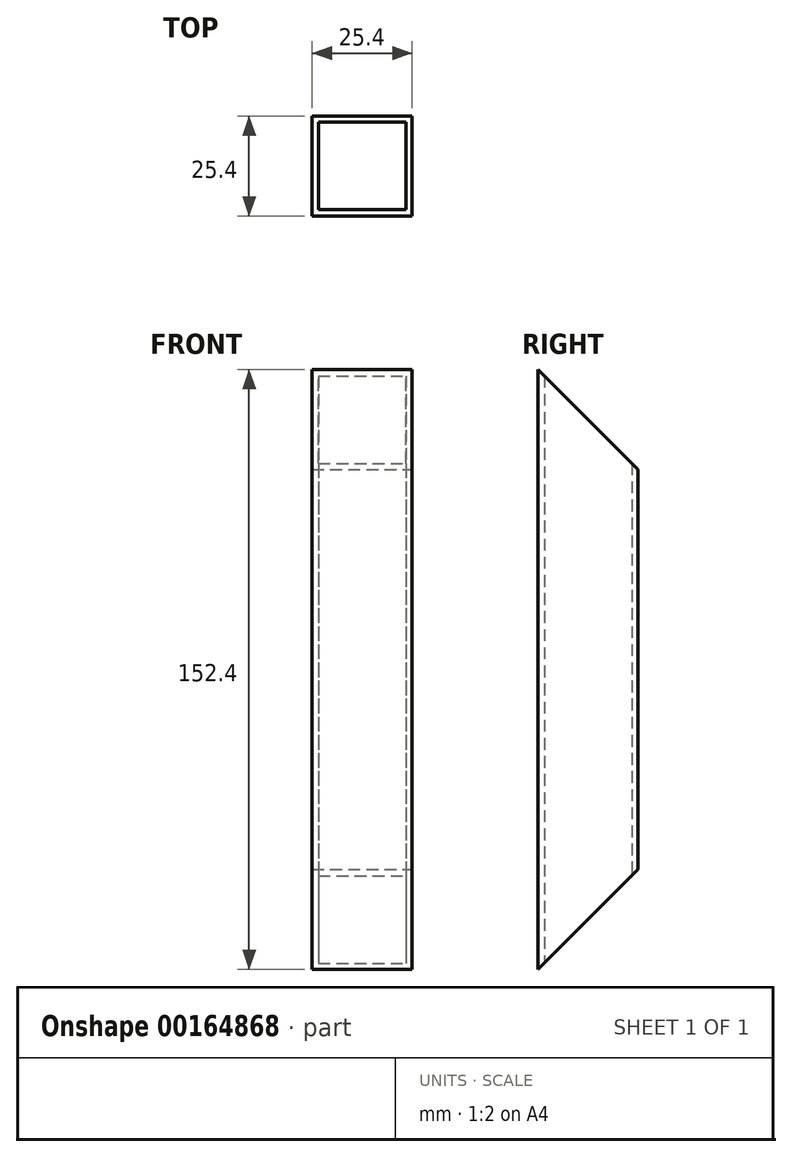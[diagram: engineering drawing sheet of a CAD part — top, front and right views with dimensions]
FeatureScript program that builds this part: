
annotation { "Feature Type Name" : "Feature", "Feature Type Description" : "" }
export const myFeature = defineFeature(function(context is Context, id is Id, definition is map)
    precondition{}
    {
        {
            var Q0;
            Q0=qCreatedBy(makeId("Top.planeOp"),FACE);
            var sketch = newSketch(context, id + "F0", { "sketchPlane" : qUnion([Q0])});
            skLineSegment(sketch, "E0.bottom", {"start": v(11.11, -11.11) * mm, "end": v(-11.11, -11.11) * mm});
            skLineSegment(sketch, "E0.top", {"start": v(11.11, 11.11) * mm, "end": v(-11.11, 11.11) * mm});
            skLineSegment(sketch, "E0.left", {"start": v(11.11, -11.11) * mm, "end": v(11.11, 11.11) * mm});
            skLineSegment(sketch, "E0.right", {"start": v(-11.11, -11.11) * mm, "end": v(-11.11, 11.11) * mm});
            skPoint(sketch, "E0.middle", {"position": v(0, 0) * mm});
            skLineSegment(sketch, "E1.bottom", {"start": v(12.7, -12.7) * mm, "end": v(-12.7, -12.7) * mm});
            skLineSegment(sketch, "E1.top", {"start": v(12.7, 12.7) * mm, "end": v(-12.7, 12.7) * mm});
            skLineSegment(sketch, "E1.left", {"start": v(12.7, -12.7) * mm, "end": v(12.7, 12.7) * mm});
            skLineSegment(sketch, "E1.right", {"start": v(-12.7, -12.7) * mm, "end": v(-12.7, 12.7) * mm});
            skSolve(sketch);
        }
        {
            var Q0;
            Q0=qSketchRegion(id+"F0",true);
            extrude(context, id + "F1", {"entities" : qUnion([Q0]), "depth" : 152.4 * mm});
        }
        {
            var Q0;
            Q0=makeQuery(id+"F1.opExtrude","SWEPT_FACE",FACE,{"disambiguationData":[OSD([sQuery(id+"F0.wireOp",EDGE,"E1.left")])]});
            var sketch = newSketch(context, id + "F2", { "sketchPlane" : qUnion([Q0])});
            skLineSegment(sketch, "E2.bottom", {"start": v(-12.7, 152.4) * mm, "end": v(12.7, 152.4) * mm});
            skLineSegment(sketch, "E2.top", {"start": v(-12.7, 127) * mm, "end": v(12.7, 127) * mm, "construction": true});
            skLineSegment(sketch, "E2.left", {"start": v(-12.7, 152.4) * mm, "end": v(-12.7, 127) * mm, "construction": true});
            skLineSegment(sketch, "E2.right", {"start": v(12.7, 152.4) * mm, "end": v(12.7, 127) * mm});
            skLineSegment(sketch, "E3", {"start": v(-12.7, 152.4) * mm, "end": v(12.7, 127) * mm});
            skLineSegment(sketch, "E4.bottom", {"start": v(-12.7, 0) * mm, "end": v(12.7, 0) * mm});
            skLineSegment(sketch, "E4.top", {"start": v(-12.7, 25.4) * mm, "end": v(12.7, 25.4) * mm, "construction": true});
            skLineSegment(sketch, "E4.left", {"start": v(-12.7, 0) * mm, "end": v(-12.7, 25.4) * mm, "construction": true});
            skLineSegment(sketch, "E4.right", {"start": v(12.7, 0) * mm, "end": v(12.7, 25.4) * mm});
            skLineSegment(sketch, "E5", {"start": v(-12.7, 0) * mm, "end": v(12.7, 25.4) * mm});
            skSolve(sketch);
        }
        {
            var Q0;
            Q0 = qSketchRegion(id + "F2", true);
            var Q1;
            Q1=makeQuery(id+"F1.opExtrude","SWEPT_FACE",FACE,{"disambiguationData":[OSD([sQuery(id+"F0.wireOp",EDGE,"E1.right")])]});
            extrude(context, id + "F3", {"entities" : qUnion([Q0]), "operationType" : NewBodyOperationType.REMOVE, "endBound" : BoundingType.UP_TO_SURFACE, "oppositeDirection" : true, "endBoundEntityFace" : qUnion([Q1]), "depth" : 25.4 * mm});
        }
    });
